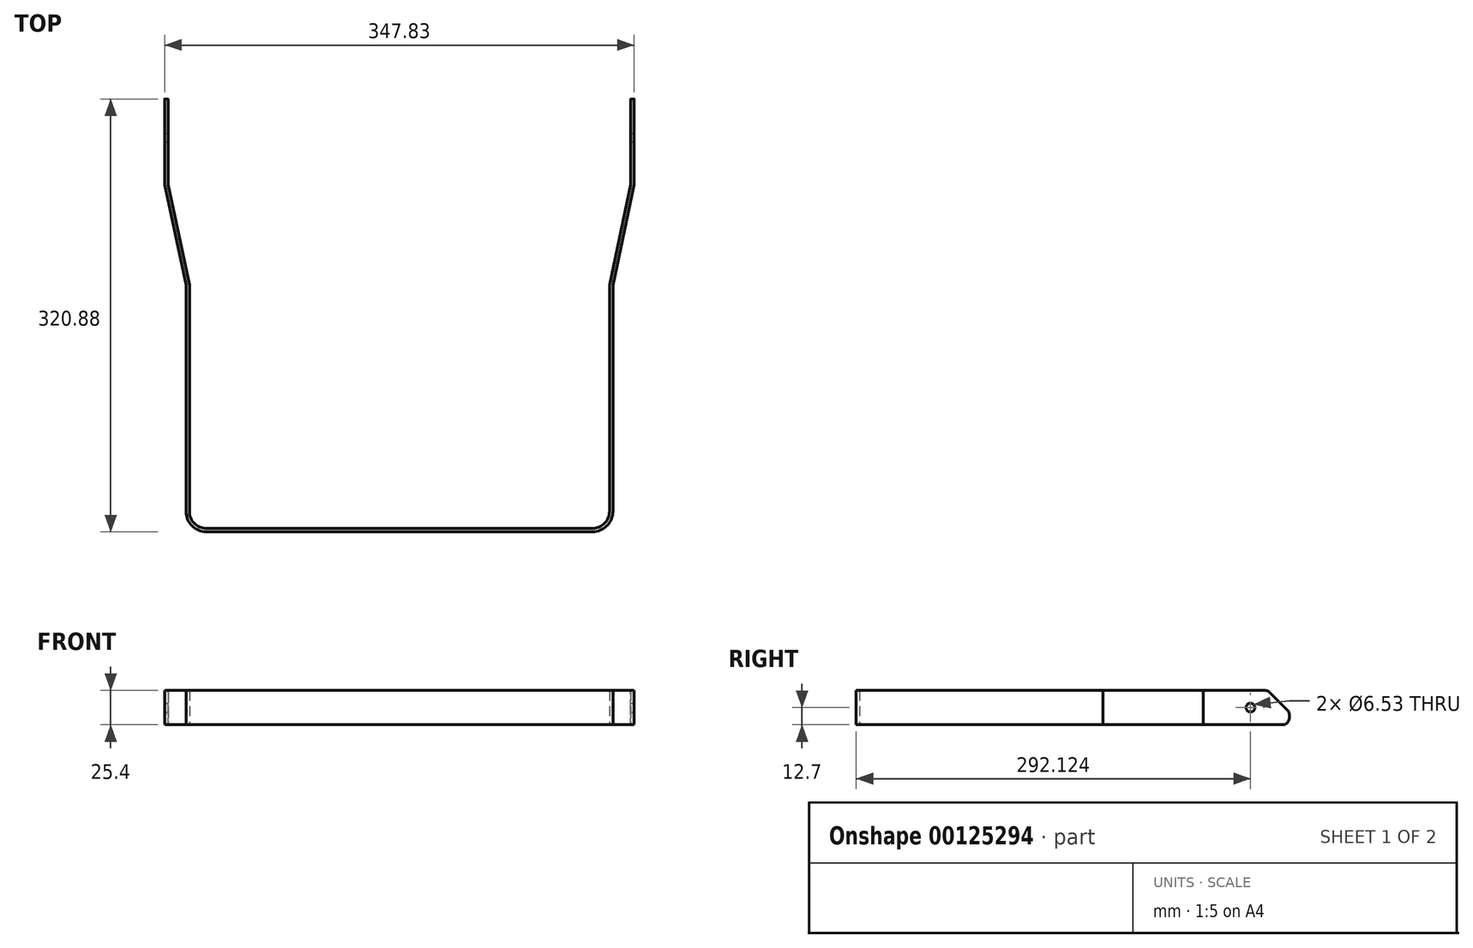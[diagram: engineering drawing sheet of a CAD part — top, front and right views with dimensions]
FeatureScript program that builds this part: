
annotation { "Feature Type Name" : "Feature", "Feature Type Description" : "" }
export const myFeature = defineFeature(function(context is Context, id is Id, definition is map)
    precondition{}
    {
        {
            var Q0;
            Q0=qCreatedBy(makeId("Top.planeOp"),FACE);
            var sketch = newSketch(context, id + "F0", { "sketchPlane" : qUnion([Q0])});
            skLineSegment(sketch, "E0", {"start": v(-65.83, 86.8) * mm, "end": v(-65.83, 23.3) * mm});
            skLineSegment(sketch, "E1", {"start": v(-65.83, 23.3) * mm, "end": v(-50.03, -51.01) * mm});
            skLineSegment(sketch, "E2", {"start": v(-50.03, -51.01) * mm, "end": v(-50.03, -218.83) * mm});
            skArc(sketch, "E3", {"start": v(-50.03, -218.83) * mm, "mid": v(-46.3, -227.8) * mm, "end": v(-37.33, -231.53) * mm});
            skLineSegment(sketch, "E4", {"start": v(-37.33, -231.53) * mm, "end": v(248.42, -231.53) * mm});
            skArc(sketch, "E5", {"start": v(248.42, -231.53) * mm, "mid": v(257.4, -227.8) * mm, "end": v(261.12, -218.83) * mm});
            skPoint(sketch, "E6", {"position": v(105.55, -231.53) * mm});
            skLineSegment(sketch, "E7.MirrorCS", {"start": v(276.92, 23.3) * mm, "end": v(261.12, -51.01) * mm});
            skLineSegment(sketch, "E8.MirrorCS", {"start": v(261.12, -51.01) * mm, "end": v(261.12, -218.83) * mm});
            skLineSegment(sketch, "E9.MirrorCS", {"start": v(276.92, 86.8) * mm, "end": v(276.92, 23.3) * mm});
            skArc(sketch, "E10.MirrorCS", {"start": v(261.12, -218.83) * mm, "mid": v(257.4, -227.8) * mm, "end": v(248.42, -231.53) * mm});
            skLineSegment(sketch, "E11.0", {"start": v(-52.57, -51.28) * mm, "end": v(-52.57, -218.83) * mm});
            skLineSegment(sketch, "E11.1", {"start": v(-68.37, 23.04) * mm, "end": v(-52.57, -51.28) * mm});
            skLineSegment(sketch, "E11.2", {"start": v(-68.37, 86.8) * mm, "end": v(-68.37, 23.04) * mm});
            skLineSegment(sketch, "E12.0", {"start": v(-37.33, -234.07) * mm, "end": v(248.42, -234.07) * mm});
            skLineSegment(sketch, "E13.0", {"start": v(263.66, -51.28) * mm, "end": v(263.66, -218.83) * mm});
            skLineSegment(sketch, "E14.0", {"start": v(279.46, 23.04) * mm, "end": v(263.66, -51.28) * mm});
            skLineSegment(sketch, "E15.0", {"start": v(279.46, 86.8) * mm, "end": v(279.46, 23.04) * mm});
            skArc(sketch, "E16", {"start": v(248.42, -234.07) * mm, "mid": v(259.2, -229.6) * mm, "end": v(263.66, -218.83) * mm});
            skArc(sketch, "E17", {"start": v(-52.57, -218.83) * mm, "mid": v(-48.1, -229.6) * mm, "end": v(-37.33, -234.07) * mm});
            skLineSegment(sketch, "E18", {"start": v(276.92, 86.8) * mm, "end": v(279.46, 86.8) * mm});
            skLineSegment(sketch, "E19", {"start": v(-68.37, 86.8) * mm, "end": v(-65.83, 86.8) * mm});
            skSolve(sketch);
        }
        {
            var Q0;
            Q0 = qSketchRegion(id + "F0", true);
            extrude(context, id + "F1", {"entities" : qUnion([Q0]), "depth" : 25.4 * mm});
        }
        {
            var Q0;
            Q0=makeQuery(id+"F1.opExtrude","SWEPT_FACE",FACE,{"disambiguationData":[OSD([sQuery(id+"F0.wireOp",EDGE,"E15.0")])]});
            var sketch = newSketch(context, id + "F2", { "sketchPlane" : qUnion([Q0])});
            skCircle(sketch, "E20", {"center": v(58.05, 12.7) * mm, "radius": 3.26 * mm});
            skSolve(sketch);
        }
        {
            var Q0;
            Q0=sQuery(id+"F2.wireOp",VERTEX,"E20.center");
            var Q1;
            Q1=makeQuery(id+"F1.opExtrude","SWEPT_BODY",BODY,{"disambiguationData":[OSD([sQuery(id+"F0.wireOp",EDGE,"E0"),sQuery(id+"F0.wireOp",EDGE,"E1"),sQuery(id+"F0.wireOp",EDGE,"E2"),sQuery(id+"F0.wireOp",EDGE,"E3"),sQuery(id+"F0.wireOp",EDGE,"E4"),sQuery(id+"F0.wireOp",EDGE,"E7.MirrorCS"),sQuery(id+"F0.wireOp",EDGE,"E8.MirrorCS"),sQuery(id+"F0.wireOp",EDGE,"E9.MirrorCS"),sQuery(id+"F0.wireOp",EDGE,"E10.MirrorCS"),sQuery(id+"F0.wireOp",EDGE,"E11.0"),sQuery(id+"F0.wireOp",EDGE,"E11.1"),sQuery(id+"F0.wireOp",EDGE,"E11.2"),sQuery(id+"F0.wireOp",EDGE,"E12.0"),sQuery(id+"F0.wireOp",EDGE,"E13.0"),sQuery(id+"F0.wireOp",EDGE,"E14.0"),sQuery(id+"F0.wireOp",EDGE,"E15.0"),sQuery(id+"F0.wireOp",EDGE,"E16"),sQuery(id+"F0.wireOp",EDGE,"E17"),sQuery(id+"F0.wireOp",EDGE,"E18"),sQuery(id+"F0.wireOp",EDGE,"E19")])]});
            hole(context, id + "F3", {"style" : HoleStyle.SIMPLE, "endStyle" : HoleEndStyle.THROUGH, "holeDiameter" : 6.53 * mm, "locations" : qUnion([Q0]), "scope" : qUnion([Q1]), "isTappedThrough" : true});
        }
        {
            var Q0;
            Q0=makeQuery(id+"F1.opExtrude","CAP_EDGE",EDGE,{"disambiguationData":[OSD([sQuery(id+"F0.wireOp",EDGE,"E18")])],"isStart":false});
            var Q1;
            Q1=makeQuery(id+"F1.opExtrude","CAP_EDGE",EDGE,{"disambiguationData":[OSD([sQuery(id+"F0.wireOp",EDGE,"E19")])],"isStart":false});
            chamfer(context, id + "F4", {"entities" : qUnion([Q0, Q1]), "chamferType" : ChamferType.OFFSET_ANGLE, "width" : 15.88 * mm, "oppositeDirection" : false, "angle" : 45 * degree, "tangentPropagation" : true});
        }
        {
            var Q0;
            {var subQ0=sQuery(id+"F0.wireOp",EDGE,"E19");Q0=makeQuery(id+"F4.opChamfer","BLEND_EDGE",EDGE,{"blendedFrom":[makeQuery(id+"F1.opExtrude","CAP_EDGE",EDGE,{"disambiguationData":[OSD([subQ0])],"isStart":false}),makeQuery(id+"F1.opExtrude","CAP_FACE",FACE,{"disambiguationData":[OSD([sQuery(id+"F0.wireOp",EDGE,"E0"),sQuery(id+"F0.wireOp",EDGE,"E1"),sQuery(id+"F0.wireOp",EDGE,"E2"),sQuery(id+"F0.wireOp",EDGE,"E3"),sQuery(id+"F0.wireOp",EDGE,"E4"),sQuery(id+"F0.wireOp",EDGE,"E7.MirrorCS"),sQuery(id+"F0.wireOp",EDGE,"E8.MirrorCS"),sQuery(id+"F0.wireOp",EDGE,"E9.MirrorCS"),sQuery(id+"F0.wireOp",EDGE,"E10.MirrorCS"),sQuery(id+"F0.wireOp",EDGE,"E11.0"),sQuery(id+"F0.wireOp",EDGE,"E11.1"),sQuery(id+"F0.wireOp",EDGE,"E11.2"),sQuery(id+"F0.wireOp",EDGE,"E12.0"),sQuery(id+"F0.wireOp",EDGE,"E13.0"),sQuery(id+"F0.wireOp",EDGE,"E14.0"),sQuery(id+"F0.wireOp",EDGE,"E15.0"),sQuery(id+"F0.wireOp",EDGE,"E16"),sQuery(id+"F0.wireOp",EDGE,"E17"),sQuery(id+"F0.wireOp",EDGE,"E18"),subQ0])],"isStart":false})],"blendedInto":[makeQuery(id+"F1.opExtrude","CAP_FACE",FACE,{"disambiguationData":[OSD([sQuery(id+"F0.wireOp",EDGE,"E0"),sQuery(id+"F0.wireOp",EDGE,"E1"),sQuery(id+"F0.wireOp",EDGE,"E2"),sQuery(id+"F0.wireOp",EDGE,"E3"),sQuery(id+"F0.wireOp",EDGE,"E4"),sQuery(id+"F0.wireOp",EDGE,"E7.MirrorCS"),sQuery(id+"F0.wireOp",EDGE,"E8.MirrorCS"),sQuery(id+"F0.wireOp",EDGE,"E9.MirrorCS"),sQuery(id+"F0.wireOp",EDGE,"E10.MirrorCS"),sQuery(id+"F0.wireOp",EDGE,"E11.0"),sQuery(id+"F0.wireOp",EDGE,"E11.1"),sQuery(id+"F0.wireOp",EDGE,"E11.2"),sQuery(id+"F0.wireOp",EDGE,"E12.0"),sQuery(id+"F0.wireOp",EDGE,"E13.0"),sQuery(id+"F0.wireOp",EDGE,"E14.0"),sQuery(id+"F0.wireOp",EDGE,"E15.0"),sQuery(id+"F0.wireOp",EDGE,"E16"),sQuery(id+"F0.wireOp",EDGE,"E17"),sQuery(id+"F0.wireOp",EDGE,"E18"),subQ0])],"isStart":false})]});}
            var Q1;
            {var subQ0=sQuery(id+"F0.wireOp",EDGE,"E18");Q1=makeQuery(id+"F4.opChamfer","BLEND_EDGE",EDGE,{"blendedFrom":[makeQuery(id+"F1.opExtrude","CAP_EDGE",EDGE,{"disambiguationData":[OSD([subQ0])],"isStart":false}),makeQuery(id+"F1.opExtrude","CAP_FACE",FACE,{"disambiguationData":[OSD([sQuery(id+"F0.wireOp",EDGE,"E0"),sQuery(id+"F0.wireOp",EDGE,"E1"),sQuery(id+"F0.wireOp",EDGE,"E2"),sQuery(id+"F0.wireOp",EDGE,"E3"),sQuery(id+"F0.wireOp",EDGE,"E4"),sQuery(id+"F0.wireOp",EDGE,"E7.MirrorCS"),sQuery(id+"F0.wireOp",EDGE,"E8.MirrorCS"),sQuery(id+"F0.wireOp",EDGE,"E9.MirrorCS"),sQuery(id+"F0.wireOp",EDGE,"E10.MirrorCS"),sQuery(id+"F0.wireOp",EDGE,"E11.0"),sQuery(id+"F0.wireOp",EDGE,"E11.1"),sQuery(id+"F0.wireOp",EDGE,"E11.2"),sQuery(id+"F0.wireOp",EDGE,"E12.0"),sQuery(id+"F0.wireOp",EDGE,"E13.0"),sQuery(id+"F0.wireOp",EDGE,"E14.0"),sQuery(id+"F0.wireOp",EDGE,"E15.0"),sQuery(id+"F0.wireOp",EDGE,"E16"),sQuery(id+"F0.wireOp",EDGE,"E17"),subQ0,sQuery(id+"F0.wireOp",EDGE,"E19")])],"isStart":false})],"blendedInto":[makeQuery(id+"F1.opExtrude","CAP_FACE",FACE,{"disambiguationData":[OSD([sQuery(id+"F0.wireOp",EDGE,"E0"),sQuery(id+"F0.wireOp",EDGE,"E1"),sQuery(id+"F0.wireOp",EDGE,"E2"),sQuery(id+"F0.wireOp",EDGE,"E3"),sQuery(id+"F0.wireOp",EDGE,"E4"),sQuery(id+"F0.wireOp",EDGE,"E7.MirrorCS"),sQuery(id+"F0.wireOp",EDGE,"E8.MirrorCS"),sQuery(id+"F0.wireOp",EDGE,"E9.MirrorCS"),sQuery(id+"F0.wireOp",EDGE,"E10.MirrorCS"),sQuery(id+"F0.wireOp",EDGE,"E11.0"),sQuery(id+"F0.wireOp",EDGE,"E11.1"),sQuery(id+"F0.wireOp",EDGE,"E11.2"),sQuery(id+"F0.wireOp",EDGE,"E12.0"),sQuery(id+"F0.wireOp",EDGE,"E13.0"),sQuery(id+"F0.wireOp",EDGE,"E14.0"),sQuery(id+"F0.wireOp",EDGE,"E15.0"),sQuery(id+"F0.wireOp",EDGE,"E16"),sQuery(id+"F0.wireOp",EDGE,"E17"),subQ0,sQuery(id+"F0.wireOp",EDGE,"E19")])],"isStart":false})]});}
            var Q2;
            {var subQ0=sQuery(id+"F0.wireOp",EDGE,"E18");Q2=makeQuery(id+"F4.opChamfer","BLEND_EDGE",EDGE,{"blendedFrom":[makeQuery(id+"F1.opExtrude","CAP_EDGE",EDGE,{"disambiguationData":[OSD([subQ0])],"isStart":false}),makeQuery(id+"F1.opExtrude","SWEPT_FACE",FACE,{"disambiguationData":[OSD([subQ0])]})],"blendedInto":[makeQuery(id+"F1.opExtrude","SWEPT_FACE",FACE,{"disambiguationData":[OSD([subQ0])]})]});}
            var Q3;
            {var subQ0=sQuery(id+"F0.wireOp",EDGE,"E19");Q3=makeQuery(id+"F4.opChamfer","BLEND_EDGE",EDGE,{"blendedFrom":[makeQuery(id+"F1.opExtrude","CAP_EDGE",EDGE,{"disambiguationData":[OSD([subQ0])],"isStart":false}),makeQuery(id+"F1.opExtrude","SWEPT_FACE",FACE,{"disambiguationData":[OSD([subQ0])]})],"blendedInto":[makeQuery(id+"F1.opExtrude","SWEPT_FACE",FACE,{"disambiguationData":[OSD([subQ0])]})]});}
            var Q4;
            Q4=makeQuery(id+"F1.opExtrude","CAP_EDGE",EDGE,{"disambiguationData":[OSD([sQuery(id+"F0.wireOp",EDGE,"E19")])],"isStart":true});
            var Q5;
            Q5=makeQuery(id+"F1.opExtrude","CAP_EDGE",EDGE,{"disambiguationData":[OSD([sQuery(id+"F0.wireOp",EDGE,"E18")])],"isStart":true});
            fillet(context, id + "F5", {"entities" : qUnion([Q0, Q1, Q2, Q3, Q4, Q5]), "radius" : 5.08 * mm, "tangentPropagation" : true, "allowEdgeOverflow" : false});
        }
    });
